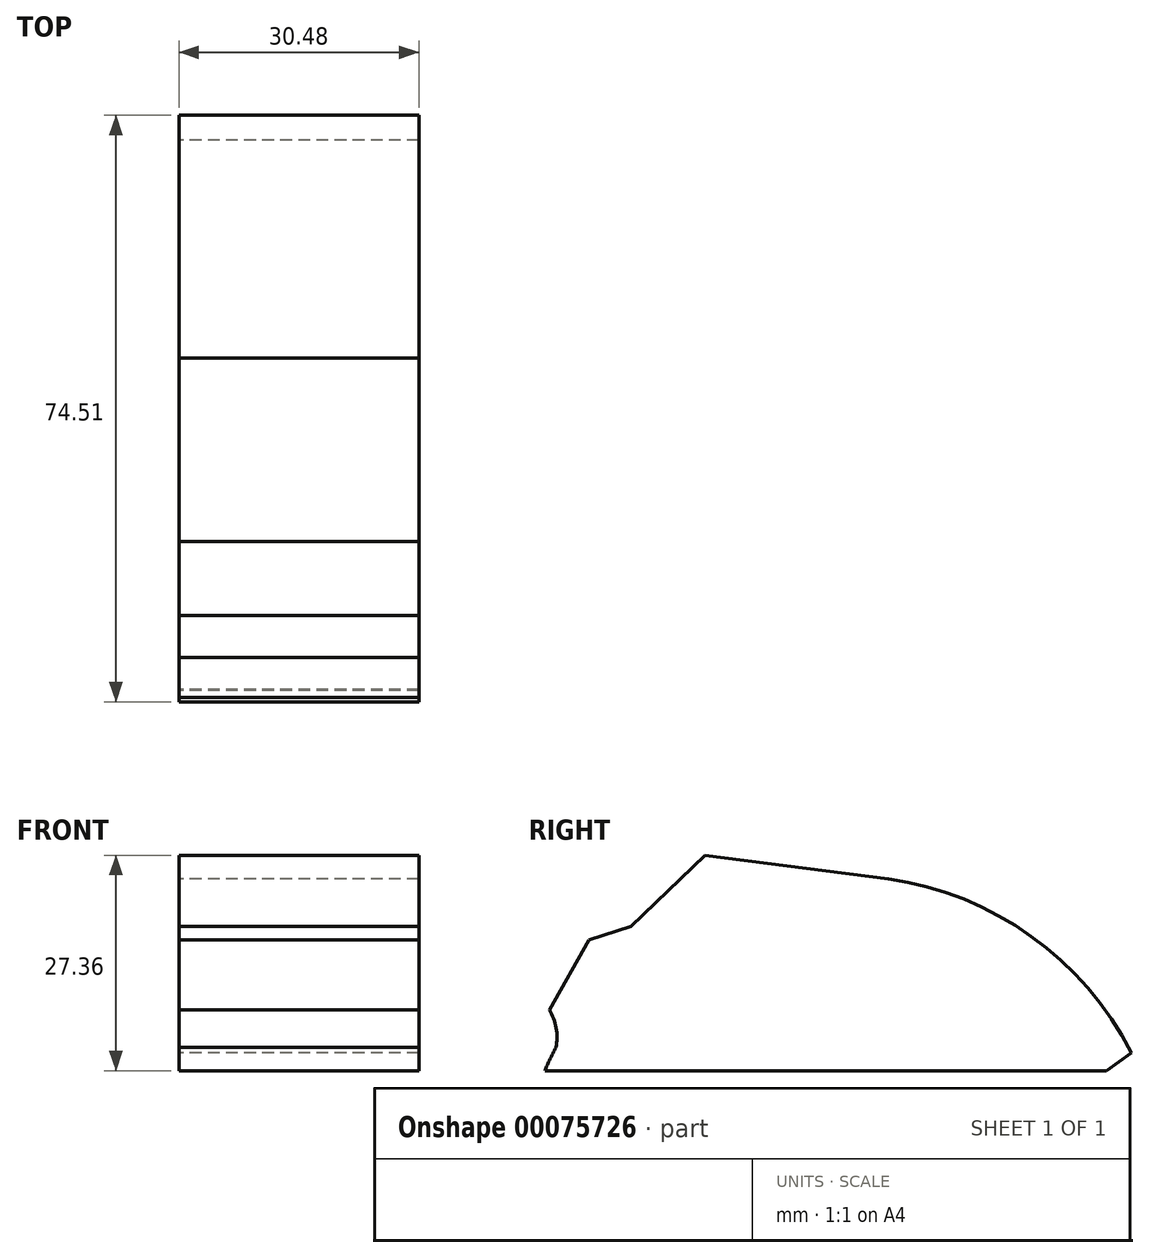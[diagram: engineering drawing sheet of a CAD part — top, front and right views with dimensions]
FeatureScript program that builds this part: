
annotation { "Feature Type Name" : "Feature", "Feature Type Description" : "" }
export const myFeature = defineFeature(function(context is Context, id is Id, definition is map)
    precondition{}
    {
        {
            var Q0;
            Q0=qCreatedBy(makeId("Right.planeOp"),FACE);
            var sketch = newSketch(context, id + "F0", { "sketchPlane" : qUnion([Q0])});
            skArc(sketch, "E0", {"start": v(-1.43, 2.27) * mm, "mid": v(-14.16, 17.08) * mm, "end": v(-32.28, 24.37) * mm});
            skLineSegment(sketch, "E1", {"start": v(-4.61, 0) * mm, "end": v(-75.94, 0) * mm});
            skLineSegment(sketch, "E2", {"start": v(-32.28, 24.37) * mm, "end": v(-55.56, 27.36) * mm});
            skLineSegment(sketch, "E3", {"start": v(-55.56, 27.36) * mm, "end": v(-64.98, 18.32) * mm});
            skLineSegment(sketch, "E4", {"start": v(-64.98, 18.32) * mm, "end": v(-70.3, 16.64) * mm});
            skLineSegment(sketch, "E5", {"start": v(-70.3, 16.64) * mm, "end": v(-75.36, 7.75) * mm});
            skArc(sketch, "E6", {"start": v(-75.94, 0) * mm, "mid": v(-74.4, 3.78) * mm, "end": v(-75.36, 7.75) * mm});
            skLineSegment(sketch, "E7", {"start": v(-9.8, 11.79) * mm, "end": v(-16.15, 9.1) * mm});
            skLineSegment(sketch, "E8", {"start": v(-16.15, 9.1) * mm, "end": v(-50.5, 12.27) * mm});
            skArc(sketch, "E9", {"start": v(-64.98, 18.32) * mm, "mid": v(-58.2, 14.19) * mm, "end": v(-50.5, 12.27) * mm});
            skArc(sketch, "E10.trimOffspring", {"start": v(-74.52, 2.93) * mm, "mid": v(-75.26, 1.48) * mm, "end": v(-75.94, 0) * mm});
            skArc(sketch, "E11", {"start": v(-32.28, 24.37) * mm, "mid": v(-42.7, 20.3) * mm, "end": v(-50.5, 12.27) * mm});
            skLineSegment(sketch, "E12", {"start": v(-1.43, 2.27) * mm, "end": v(-4.61, 0) * mm});
            skLineSegment(sketch, "E13", {"start": v(-4.61, 0) * mm, "end": v(-57.48, 3.9) * mm});
            skLineSegment(sketch, "E14", {"start": v(-57.48, 3.9) * mm, "end": v(-60.17, 0) * mm});
            skArc(sketch, "E15", {"start": v(-50.5, 12.27) * mm, "mid": v(-55.18, 9.08) * mm, "end": v(-57.48, 3.9) * mm});
            skArc(sketch, "E16", {"start": v(-61.9, 6.4) * mm, "mid": v(-68.56, 7.8) * mm, "end": v(-75.36, 7.75) * mm});
            skArc(sketch, "E17", {"start": v(-16.15, 9.1) * mm, "mid": v(-15.11, 11.23) * mm, "end": v(-15.76, 13.52) * mm});
            skArc(sketch, "E18", {"start": v(-15.76, 13.52) * mm, "mid": v(-22.47, 20.7) * mm, "end": v(-31.62, 24.27) * mm});
            skSolve(sketch);
        }
        {
            var Q0;
            Q0=makeQuery(id+"F0.imprint","IMPRINT",FACE,{"disambiguationData":[TD([[makeQuery(id+"F0.imprint","IMPRINT",EDGE,{"derivedFrom":sQuery(id+"F0.wireOp",EDGE,"E8")}),1.0]])]});
            var Q1;
            {var subQ0=sQuery(id+"F0.wireOp",EDGE,"E18");var subQ1=sQuery(id+"F0.wireOp",EDGE,"E0");var subQ2=makeQuery(id+"F0.imprint","INTERSECT",VERTEX,{"disambiguationData":[OD(0.0)],"derivedFrom":[subQ1,subQ0]});Q1=makeQuery(id+"F0.imprint","IMPRINT",FACE,{"disambiguationData":[TD([[makeQuery(id+"F0.imprint","IMPRINT",EDGE,{"disambiguationData":[TD([[subQ2,1.0]])],"derivedFrom":subQ1}),-1.0]])]});}
            var Q2;
            {var subQ0=sQuery(id+"F0.wireOp",EDGE,"E10.trimOffspring");Q2=makeQuery(id+"F0.imprint","IMPRINT",FACE,{"disambiguationData":[TD([[makeQuery(id+"F0.imprint","IMPRINT",EDGE,{"derivedFrom":subQ0}),1.0]])]});}
            var Q3;
            {var subQ0=sQuery(id+"F0.wireOp",EDGE,"E13");Q3=makeQuery(id+"F0.imprint","IMPRINT",FACE,{"disambiguationData":[TD([[makeQuery(id+"F0.imprint","IMPRINT",EDGE,{"derivedFrom":subQ0}),1.0]])]});}
            var Q4;
            Q4=makeQuery(id+"F0.imprint","IMPRINT",FACE,{"disambiguationData":[TD([[makeQuery(id+"F0.imprint","IMPRINT",EDGE,{"derivedFrom":sQuery(id+"F0.wireOp",EDGE,"E2")}),1.0]])]});
            var Q5;
            Q5=makeQuery(id+"F0.imprint","IMPRINT",FACE,{"disambiguationData":[TD([[makeQuery(id+"F0.imprint","IMPRINT",EDGE,{"derivedFrom":sQuery(id+"F0.wireOp",EDGE,"E8")}),-1.0]])]});
            var Q6;
            Q6=makeQuery(id+"F0.imprint","IMPRINT",FACE,{"disambiguationData":[TD([[makeQuery(id+"F0.imprint","IMPRINT",EDGE,{"derivedFrom":sQuery(id+"F0.wireOp",EDGE,"E4")}),1.0]])]});
            extrude(context, id + "F1", {"entities" : qUnion([Q0, Q1, Q2, Q3, Q4, Q5, Q6]), "depth" : 15.24 * mm, "hasSecondDirection" : true, "secondDirectionOppositeDirection" : true, "secondDirectionDepth" : 15.24 * mm});
        }
    });
